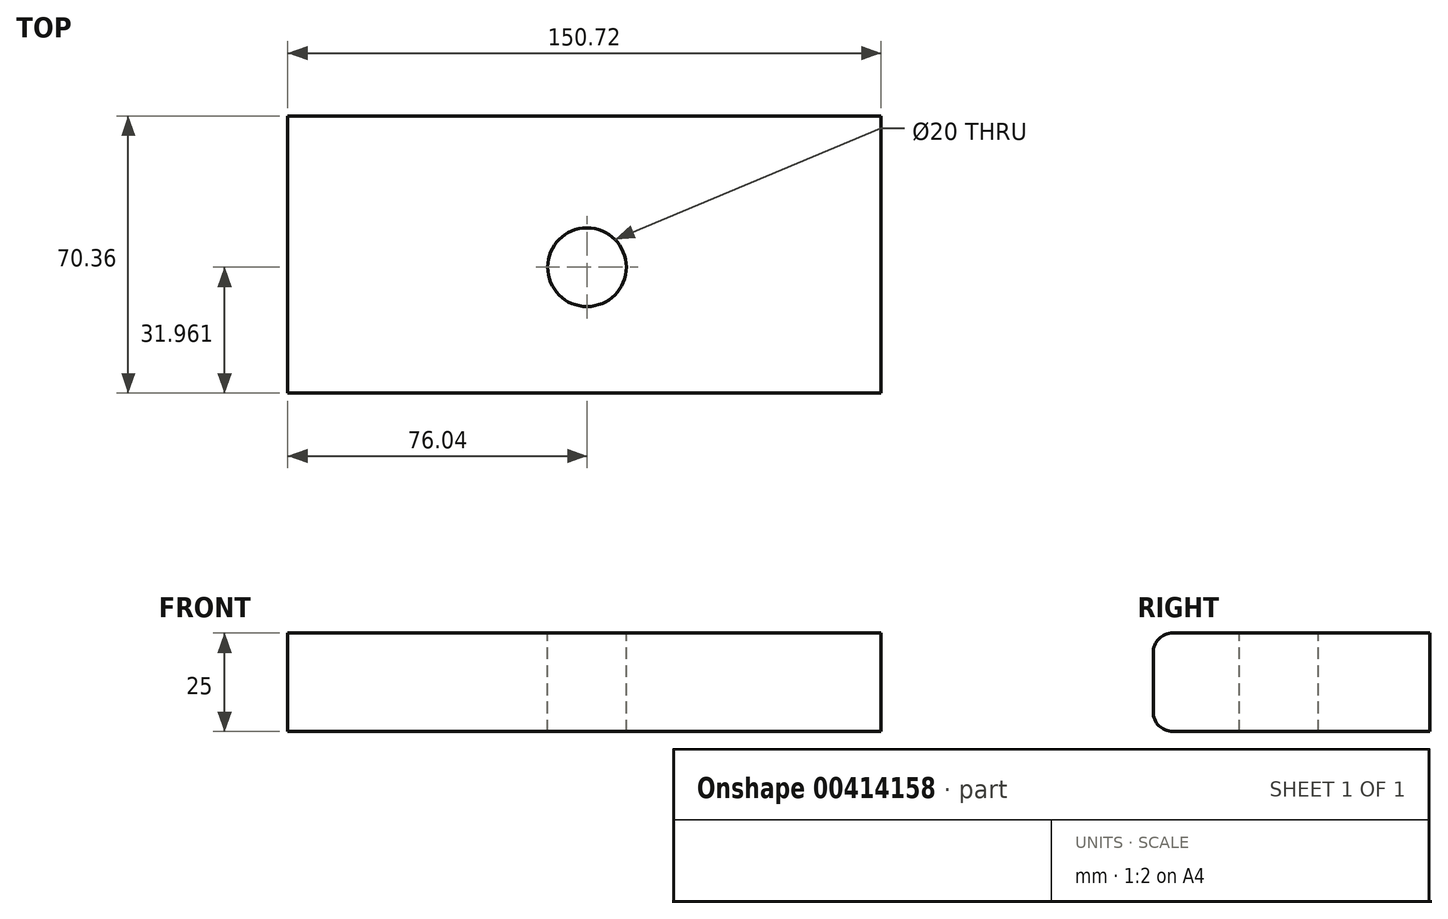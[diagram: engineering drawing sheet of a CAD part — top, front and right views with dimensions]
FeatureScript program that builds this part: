
annotation { "Feature Type Name" : "Feature", "Feature Type Description" : "" }
export const myFeature = defineFeature(function(context is Context, id is Id, definition is map)
    precondition{}
    {
        {
            var Q0;
            Q0=qCreatedBy(makeId("Top.planeOp"),FACE);
            var sketch = newSketch(context, id + "F0", { "sketchPlane" : qUnion([Q0])});
            skLineSegment(sketch, "E0.bottom", {"start": v(-75.36, 35.18) * mm, "end": v(75.36, 35.18) * mm});
            skLineSegment(sketch, "E0.top", {"start": v(-75.36, -35.18) * mm, "end": v(75.36, -35.18) * mm});
            skLineSegment(sketch, "E0.left", {"start": v(-75.36, 35.18) * mm, "end": v(-75.36, -35.18) * mm});
            skLineSegment(sketch, "E0.right", {"start": v(75.36, 35.18) * mm, "end": v(75.36, -35.18) * mm});
            skPoint(sketch, "E0.middle", {"position": v(0, 0) * mm});
            skSolve(sketch);
        }
        {
            var Q0;
            Q0 = qSketchRegion(id + "F0", true);
            extrude(context, id + "F1", {"entities" : qUnion([Q0]), "depth" : 25 * mm});
        }
        {
            var Q0;
            Q0=makeQuery(id+"F1.opExtrude","CAP_EDGE",EDGE,{"disambiguationData":[OSD([sQuery(id+"F0.wireOp",EDGE,"E0.top")])],"isStart":false});
            fillet(context, id + "F2", {"entities" : qUnion([Q0]), "radius" : 5 * mm, "tangentPropagation" : true, "allowEdgeOverflow" : false});
        }
        {
            var Q0;
            Q0=makeQuery(id+"F1.opExtrude","CAP_EDGE",EDGE,{"disambiguationData":[OSD([sQuery(id+"F0.wireOp",EDGE,"E0.top")])],"isStart":true});
            fillet(context, id + "F3", {"entities" : qUnion([Q0]), "radius" : 5 * mm, "tangentPropagation" : true, "allowEdgeOverflow" : false});
        }
        {
            var Q0;
            Q0=makeQuery(id+"F1.opExtrude","CAP_FACE",FACE,{"disambiguationData":[OSD([sQuery(id+"F0.wireOp",EDGE,"E0.bottom"),sQuery(id+"F0.wireOp",EDGE,"E0.top"),sQuery(id+"F0.wireOp",EDGE,"E0.left"),sQuery(id+"F0.wireOp",EDGE,"E0.right")])],"isStart":false});
            var sketch = newSketch(context, id + "F4", { "sketchPlane" : qUnion([Q0])});
            skPoint(sketch, "E1", {"position": v(0.68, -3.22) * mm});
            skPoint(sketch, "E2", {"position": v(103.06, 41.62) * mm});
            skSolve(sketch);
        }
        {
            var Q0;
            Q0=sQuery(id+"F4.wireOp",VERTEX,"E1");
            var Q1;
            Q1=makeQuery(id+"F1.opExtrude","SWEPT_BODY",BODY,{"disambiguationData":[OSD([sQuery(id+"F0.wireOp",EDGE,"E0.bottom"),sQuery(id+"F0.wireOp",EDGE,"E0.top"),sQuery(id+"F0.wireOp",EDGE,"E0.left"),sQuery(id+"F0.wireOp",EDGE,"E0.right")])]});
            hole(context, id + "F5", {"style" : HoleStyle.SIMPLE, "endStyle" : HoleEndStyle.THROUGH, "holeDiameter" : 20 * mm, "isTappedThrough" : true, "tappedDepth" : 12 * mm, "tapClearance" : 3, "locations" : qUnion([Q0]), "scope" : qUnion([Q1])});
        }
    });
